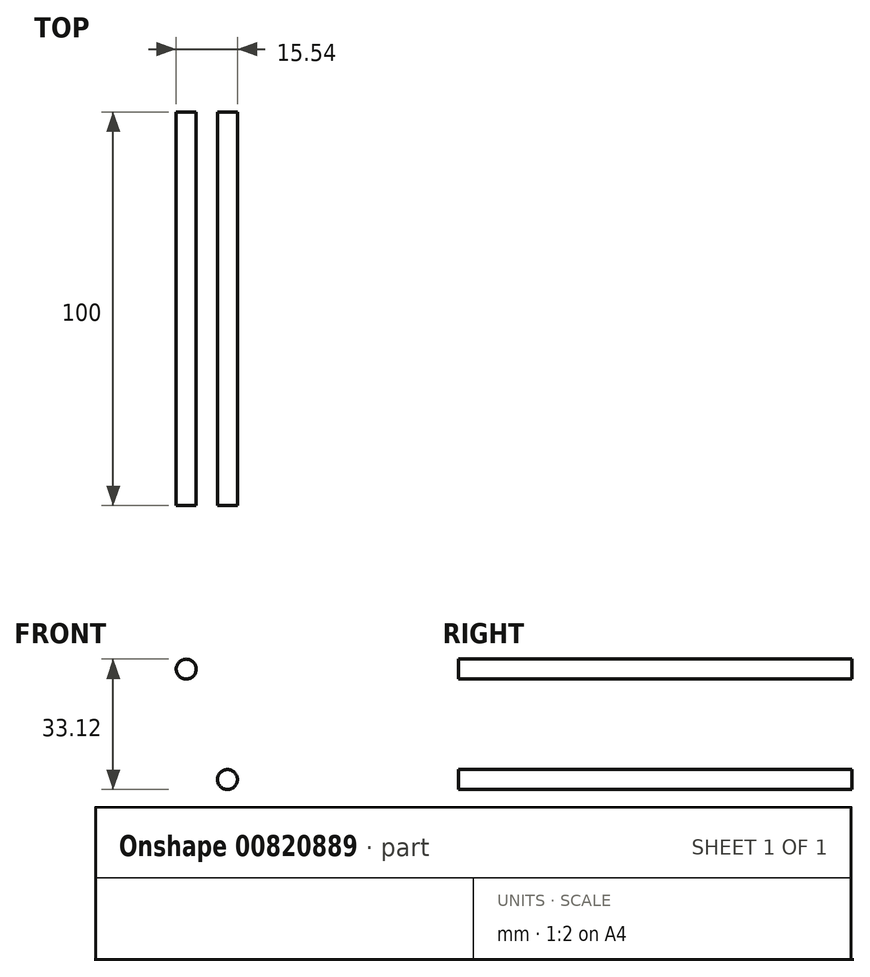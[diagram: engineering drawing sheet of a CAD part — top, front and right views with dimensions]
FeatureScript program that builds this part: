
annotation { "Feature Type Name" : "Feature", "Feature Type Description" : "" }
export const myFeature = defineFeature(function(context is Context, id is Id, definition is map)
    precondition{}
    {
        {
            var Q0;
            Q0=qCreatedBy(makeId("Front.planeOp"),FACE);
            var sketch = newSketch(context, id + "F0", { "sketchPlane" : qUnion([Q0])});
            skCircle(sketch, "E0", {"center": v(0, 0) * mm, "radius": 20 * mm});
            skSolve(sketch);
        }
        {
            var Q0;
            Q0=makeQuery(id+"F0.imprint","IMPRINT",FACE,{"disambiguationData":[TD([[makeQuery(id+"F0.imprint","IMPRINT",EDGE,{"derivedFrom":sQuery(id+"F0.wireOp",EDGE,"E0")}),1.0]])]});
            extrude(context, id + "F1", {"entities" : qUnion([Q0]), "endBound" : BoundingType.SYMMETRIC, "depth" : 100 * mm, "offsetDistance" : 25 * mm});
        }
        {
            var Q0;
            Q0=qCreatedBy(makeId("Front.planeOp"),FACE);
            cPlane(context, id + "F2", {"entities" : qUnion([Q0]), "cplaneType" : CPlaneType.OFFSET, "offset" : 60 * mm, "width" : 150 * mm, "height" : 150 * mm});
        }
        {
            var Q0;
            Q0=qCreatedBy(id+"F2.planeOp",FACE);
            var sketch = newSketch(context, id + "F3", { "sketchPlane" : qUnion([Q0])});
            skCircle(sketch, "E1", {"center": v(0, 0) * mm, "radius": 10 * mm});
            skSolve(sketch);
        }
        {
            var Q0;
            Q0=makeQuery(id+"F3.imprint","IMPRINT",FACE,{"disambiguationData":[TD([[makeQuery(id+"F3.imprint","IMPRINT",EDGE,{"derivedFrom":sQuery(id+"F3.wireOp",EDGE,"E1")}),1.0]])]});
            extrude(context, id + "F4", {"entities" : qUnion([Q0]), "operationType" : NewBodyOperationType.REMOVE, "oppositeDirection" : true, "depth" : 120 * mm, "offsetDistance" : 25 * mm});
        }
        {
            var Q0;
            Q0=qCreatedBy(makeId("Right.planeOp"),FACE);
            cPlane(context, id + "F5", {"entities" : qUnion([Q0]), "cplaneType" : CPlaneType.OFFSET, "offset" : 30 * mm, "width" : 150 * mm, "height" : 150 * mm});
        }
        {
            var Q0;
            Q0=qCreatedBy(id+"F5.planeOp",FACE);
            var sketch = newSketch(context, id + "F6", { "sketchPlane" : qUnion([Q0])});
            skCircle(sketch, "E2", {"center": v(0, 0) * mm, "radius": 10 * mm});
            skSolve(sketch);
        }
        {
            var Q0;
            Q0=makeQuery(id+"F6.imprint","IMPRINT",FACE,{"disambiguationData":[TD([[makeQuery(id+"F6.imprint","IMPRINT",EDGE,{"derivedFrom":sQuery(id+"F6.wireOp",EDGE,"E2")}),1.0]])]});
            extrude(context, id + "F7", {"entities" : qUnion([Q0]), "operationType" : NewBodyOperationType.REMOVE, "endBound" : BoundingType.SYMMETRIC, "oppositeDirection" : true, "depth" : 100 * mm, "offsetDistance" : 25 * mm});
        }
        {
            var Q0;
            Q0=makeQuery(id+"F1.opExtrude","CAP_FACE",FACE,{"disambiguationData":[OSD([sQuery(id+"F0.wireOp",EDGE,"E0")])],"isStart":false});
            var sketch = newSketch(context, id + "F8", { "sketchPlane" : qUnion([Q0])});
            skCircle(sketch, "E3", {"center": v(5.24, 14.02) * mm, "radius": 2.53 * mm});
            skLineSegment(sketch, "E4", {"start": v(-74.08, 0) * mm, "end": v(84.27, 0) * mm, "construction": true});
            skCircle(sketch, "E5.MirrorC", {"center": v(5.24, -14.02) * mm, "radius": 2.53 * mm});
            skLineSegment(sketch, "E6", {"start": v(0, 53.11) * mm, "end": v(0, -46.32) * mm, "construction": true});
            skCircle(sketch, "E7.MirrorC", {"center": v(-5.24, 14.02) * mm, "radius": 2.53 * mm});
            skCircle(sketch, "E8.MirrorC", {"center": v(-5.24, -14.02) * mm, "radius": 2.53 * mm});
            skSolve(sketch);
        }
        {
            var Q0;
            Q0=makeQuery(id+"F8.imprint","IMPRINT",FACE,{"disambiguationData":[TD([[makeQuery(id+"F8.imprint","IMPRINT",EDGE,{"derivedFrom":sQuery(id+"F8.wireOp",EDGE,"E3")}),1.0]])]});
            extrude(context, id + "F9", {"entities" : qUnion([Q0]), "operationType" : NewBodyOperationType.REMOVE, "oppositeDirection" : true, "depth" : 101 * mm, "offsetDistance" : 25 * mm});
        }
        {
            var Q0;
            Q0=makeQuery(id+"F8.imprint","IMPRINT",FACE,{"disambiguationData":[TD([[makeQuery(id+"F8.imprint","IMPRINT",EDGE,{"derivedFrom":sQuery(id+"F8.wireOp",EDGE,"E7.MirrorC")}),-1.0]])]});
            var Q1;
            Q1=makeQuery(id+"F8.imprint","IMPRINT",FACE,{"disambiguationData":[TD([[makeQuery(id+"F8.imprint","IMPRINT",EDGE,{"derivedFrom":sQuery(id+"F8.wireOp",EDGE,"E8.MirrorC")}),1.0]])]});
            var Q2;
            Q2=makeQuery(id+"F8.imprint","IMPRINT",FACE,{"disambiguationData":[TD([[makeQuery(id+"F8.imprint","IMPRINT",EDGE,{"derivedFrom":sQuery(id+"F8.wireOp",EDGE,"E5.MirrorC")}),-1.0]])]});
            extrude(context, id + "F10", {"entities" : qUnion([Q0, Q1, Q2]), "operationType" : NewBodyOperationType.REMOVE, "oppositeDirection" : true, "depth" : 101 * mm, "offsetDistance" : 25 * mm});
        }
    });
